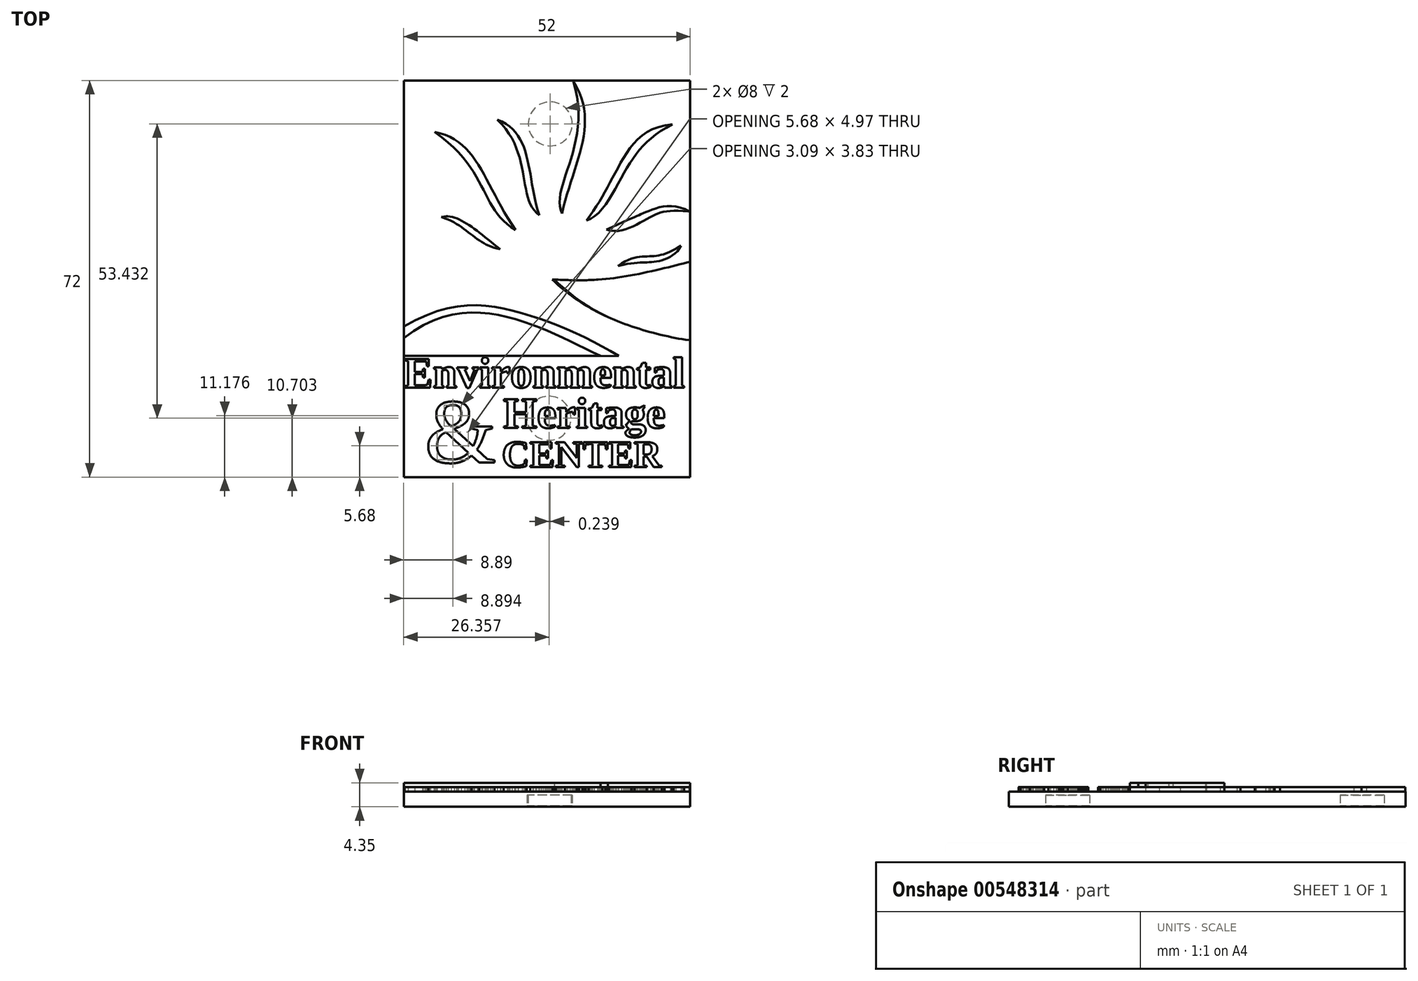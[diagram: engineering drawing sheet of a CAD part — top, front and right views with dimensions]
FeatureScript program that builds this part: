
annotation { "Feature Type Name" : "Feature", "Feature Type Description" : "" }
export const myFeature = defineFeature(function(context is Context, id is Id, definition is map)
    precondition{}
    {
        {
            var Q0;
            Q0=qCreatedBy(makeId("Top.planeOp"),FACE);
            var sketch = newSketch(context, id + "F0", { "sketchPlane" : qUnion([Q0])});
            skFitSpline(sketch, "E0", {"points": [v(4.31, 44.96) * mm, v(2.38, 20.78) * mm], "startDerivative": vector(14.8, -23.62) * mm, "endDerivative": vector(-6, -27.25) * mm});
            skFitSpline(sketch, "E1", {"points": [v(4.31, 45.15) * mm, v(2.38, 20.78) * mm], "startDerivative": vector(10.64, -35.08) * mm, "endDerivative": vector(7.02, -14.4) * mm});
            skFitSpline(sketch, "E2", {"points": [v(-9.33, 37.79) * mm, v(-1.76, 20.42) * mm], "startDerivative": vector(19.64, -7.65) * mm, "endDerivative": vector(7, -21.6) * mm});
            skFitSpline(sketch, "E3", {"points": [v(-9.33, 37.79) * mm, v(-1.76, 20.42) * mm], "startDerivative": vector(19.52, -19.07) * mm, "endDerivative": vector(12.52, -9.58) * mm});
            skFitSpline(sketch, "E4", {"points": [v(-20.73, 35.54) * mm, v(-6.05, 17.77) * mm], "startDerivative": vector(23.87, -4.4) * mm, "endDerivative": vector(17.15, -24.68) * mm});
            skFitSpline(sketch, "E5", {"points": [v(-20.73, 35.54) * mm, v(-6.05, 17.77) * mm], "startDerivative": vector(30.6, -21.67) * mm, "endDerivative": vector(19.93, -11.59) * mm});
            skFitSpline(sketch, "E6", {"points": [v(-19.49, 20.1) * mm, v(-8.88, 14.3) * mm], "startDerivative": vector(8.74, 2.48) * mm, "endDerivative": vector(12.97, -10.2) * mm});
            skFitSpline(sketch, "E7", {"points": [v(-19.49, 20.1) * mm, v(-8.88, 14.3) * mm], "startDerivative": vector(14.35, -4.5) * mm, "endDerivative": vector(12.97, -1.93) * mm});
            skFitSpline(sketch, "E8", {"points": [v(22.42, 36.91) * mm, v(12.63, 29.23) * mm, v(6.82, 19.5) * mm], "startDerivative": vector(-32.02, -1.89) * mm, "endDerivative": vector(-15.34, -19.87) * mm});
            skFitSpline(sketch, "E9", {"points": [v(22.42, 36.91) * mm, v(13.78, 28.37) * mm, v(6.82, 19.5) * mm], "startDerivative": vector(-26.44, -13.49) * mm, "endDerivative": vector(-18.51, -5.76) * mm});
            skFitSpline(sketch, "E10", {"points": [v(10.44, 17.8) * mm, v(17.32, 20.88) * mm, v(25.87, 20.74) * mm], "startDerivative": vector(29.68, 13.68) * mm, "endDerivative": vector(18.14, -14.7) * mm});
            skFitSpline(sketch, "E11", {"points": [v(10.44, 17.8) * mm, v(18.21, 19.99) * mm, v(25.38, 21.1) * mm], "startDerivative": vector(15.53, -5.4) * mm, "endDerivative": vector(24.63, -2.44) * mm});
            skFitSpline(sketch, "E12", {"points": [v(12.53, 11.24) * mm, v(18.58, 12.99) * mm, v(23.97, 14.92) * mm], "startDerivative": vector(15.39, 11.11) * mm, "endDerivative": vector(14.79, 9.41) * mm});
            skFitSpline(sketch, "E13", {"points": [v(12.53, 11.24) * mm, v(18.98, 11.97) * mm, v(23.97, 14.92) * mm], "startDerivative": vector(21.7, 4.9) * mm, "endDerivative": vector(6.08, 13.06) * mm});
            skFitSpline(sketch, "E14", {"points": [v(0.27, 8.75) * mm, v(10.37, 1.93) * mm, v(25.63, -2.36) * mm], "startDerivative": vector(17.78, -17.12) * mm, "endDerivative": vector(27.14, -3.63) * mm});
            skFitSpline(sketch, "E15", {"points": [v(-1.66, 8.98) * mm, v(10.04, 0.8) * mm, v(25.63, -3.6) * mm], "startDerivative": vector(19.98, -21.9) * mm, "endDerivative": vector(27.82, -3.65) * mm});
            skFitSpline(sketch, "E16", {"points": [v(0.27, 8.75) * mm, v(12.27, 9.1) * mm, v(25.68, 12.08) * mm], "startDerivative": vector(25.56, -1.26) * mm, "endDerivative": vector(20.03, 5.21) * mm});
            skFitSpline(sketch, "E17", {"points": [v(-26.4, 0.32) * mm, v(-5.28, 2.75) * mm, v(12.45, -5.04) * mm], "startDerivative": vector(42.56, 27.28) * mm, "endDerivative": vector(34.62, -19.88) * mm});
            skFitSpline(sketch, "E18", {"points": [v(-26.4, -2.02) * mm, v(-5.58, 1.45) * mm, v(9.78, -5.04) * mm], "startDerivative": vector(33.71, 28.86) * mm, "endDerivative": vector(32.46, -15.17) * mm});
            skFitSpline(sketch, "E19", {"points": [v(-26.4, 19.28) * mm, v(-13.06, 11.61) * mm, v(-1.66, 8.98) * mm], "startDerivative": vector(29.42, -19.76) * mm, "endDerivative": vector(24.53, -2.4) * mm});
            skFitSpline(sketch, "E20", {"points": [v(-8, 10.03) * mm, v(0.62, 16.74) * mm, v(8.95, 8.75) * mm], "startDerivative": vector(8.7, 30.35) * mm, "endDerivative": vector(2.28, -31.65) * mm});
            skLineSegment(sketch, "E21", {"start": v(-26.4, 44.96) * mm, "end": v(-26.4, -5.04) * mm});
            skLineSegment(sketch, "E22", {"start": v(-26.4, 44.96) * mm, "end": v(4.33, 44.96) * mm});
            skLineSegment(sketch, "E23", {"start": v(-26.4, -5.04) * mm, "end": v(25.6, -5.04) * mm});
            skLineSegment(sketch, "E24.trimOffspring", {"start": v(4.33, 44.96) * mm, "end": v(25.6, 44.96) * mm});
            skLineSegment(sketch, "E25", {"start": v(25.6, 44.96) * mm, "end": v(25.6, -5.04) * mm});
            skText(sketch, "E26", { "text": "Environmental", "fontName": "Tinos-Regular.ttf"});
            skText(sketch, "E27", { "text": "Heritage", "fontName": "Tinos-Regular.ttf"});
            skText(sketch, "E28", { "text": "C E N T E R", "fontName": "Tinos-Regular.ttf"});
            skText(sketch, "E29", { "text": "&", "fontName": "Tinos-Regular.ttf"});
            skLineSegment(sketch, "E30", {"start": v(-26.4, -5.04) * mm, "end": v(-26.4, -27.04) * mm});
            skLineSegment(sketch, "E31", {"start": v(25.6, -5.04) * mm, "end": v(25.6, -27.04) * mm});
            skLineSegment(sketch, "E32", {"start": v(-26.4, -27.04) * mm, "end": v(25.6, -27.04) * mm});
            const initialGuessF0  = {"E26": [-0.0253, -0.01139, 1, 0, 0.006], "E27": [-0.00842, -0.0183, 1, 0, 0.006], "E28": [-0.0084, -0.0244, 1, 0, 0.004], "E29": [-0.02253, -0.02446, 1, 0, 0.012]};
            skSetInitialGuess(sketch, initialGuessF0);
            skSolve(sketch);
        }
        {
            var Q0;
            Q0=makeQuery(id+"F0.imprint","IMPRINT",FACE,{"disambiguationData":[TD([[makeQuery(id+"F0.imprint","IMPRINT",EDGE,{"derivedFrom":sQuery(id+"F0.wireOp",EDGE,"E26.sketch_text.stroke-270")}),1.0]])]});
            var Q1;
            Q1=makeQuery(id+"F0.imprint","IMPRINT",FACE,{"disambiguationData":[TD([[makeQuery(id+"F0.imprint","IMPRINT",EDGE,{"derivedFrom":sQuery(id+"F0.wireOp",EDGE,"E10")}),-1.0]])]});
            var Q2;
            Q2=makeQuery(id+"F0.imprint","IMPRINT",FACE,{"disambiguationData":[TD([[makeQuery(id+"F0.imprint","IMPRINT",EDGE,{"derivedFrom":sQuery(id+"F0.wireOp",EDGE,"E26.sketch_text.stroke-205")}),-1.0]])]});
            var Q3;
            Q3=makeQuery(id+"F0.imprint","IMPRINT",FACE,{"disambiguationData":[TD([[makeQuery(id+"F0.imprint","IMPRINT",EDGE,{"derivedFrom":sQuery(id+"F0.wireOp",EDGE,"E26.sketch_text.stroke-200")}),1.0]])]});
            var Q4;
            Q4=makeQuery(id+"F0.imprint","IMPRINT",FACE,{"disambiguationData":[TD([[makeQuery(id+"F0.imprint","IMPRINT",EDGE,{"derivedFrom":sQuery(id+"F0.wireOp",EDGE,"E26.sketch_text.stroke-51")}),-1.0]])]});
            var Q5;
            {var subQ1=sQuery(id+"F0.wireOp",EDGE,"E15");Q5=makeQuery(id+"F0.imprint","IMPRINT",FACE,{"disambiguationData":[TD([[makeQuery(id+"F0.imprint","IMPRINT",EDGE,{"derivedFrom":subQ1}),-1.0]])]});}
            var Q6;
            Q6=makeQuery(id+"F0.imprint","IMPRINT",FACE,{"disambiguationData":[TD([[makeQuery(id+"F0.imprint","IMPRINT",EDGE,{"derivedFrom":sQuery(id+"F0.wireOp",EDGE,"E27.sketch_text.stroke-161")}),1.0]])]});
            var Q7;
            Q7=makeQuery(id+"F0.imprint","IMPRINT",FACE,{"disambiguationData":[TD([[makeQuery(id+"F0.imprint","IMPRINT",EDGE,{"derivedFrom":sQuery(id+"F0.wireOp",EDGE,"E26.sketch_text.stroke-103")}),-1.0]])]});
            var Q8;
            {var subQ0=sQuery(id+"F0.wireOp",EDGE,"E1");var subQ1=sQuery(id+"F0.wireOp",EDGE,"E0");var subQ2=makeQuery(id+"F0.imprint","INTERSECT",VERTEX,{"disambiguationData":[OD(0.0)],"derivedFrom":[subQ1,subQ0]});Q8=makeQuery(id+"F0.imprint","IMPRINT",FACE,{"disambiguationData":[TD([[makeQuery(id+"F0.imprint","IMPRINT",EDGE,{"disambiguationData":[TD([[subQ2,1.0]])],"derivedFrom":subQ1}),-1.0]])]});}
            var Q9;
            Q9=makeQuery(id+"F0.imprint","IMPRINT",FACE,{"disambiguationData":[TD([[makeQuery(id+"F0.imprint","IMPRINT",EDGE,{"derivedFrom":sQuery(id+"F0.wireOp",EDGE,"E4")}),-1.0]])]});
            var Q10;
            Q10=makeQuery(id+"F0.imprint","IMPRINT",FACE,{"disambiguationData":[TD([[makeQuery(id+"F0.imprint","IMPRINT",EDGE,{"derivedFrom":sQuery(id+"F0.wireOp",EDGE,"E2")}),-1.0]])]});
            var Q11;
            {var subQ4=sQuery(id+"F0.wireOp",EDGE,"E14");Q11=makeQuery(id+"F0.imprint","IMPRINT",FACE,{"disambiguationData":[TD([[makeQuery(id+"F0.imprint","IMPRINT",EDGE,{"derivedFrom":subQ4}),-1.0]])]});}
            var Q12;
            Q12=makeQuery(id+"F0.imprint","IMPRINT",FACE,{"disambiguationData":[TD([[makeQuery(id+"F0.imprint","IMPRINT",EDGE,{"derivedFrom":sQuery(id+"F0.wireOp",EDGE,"E26.sketch_text.stroke-26")}),-1.0]])]});
            var Q13;
            Q13=makeQuery(id+"F0.imprint","IMPRINT",FACE,{"disambiguationData":[TD([[makeQuery(id+"F0.imprint","IMPRINT",EDGE,{"derivedFrom":sQuery(id+"F0.wireOp",EDGE,"E29.sketch_text.stroke-0")}),-1.0]])]});
            var Q14;
            Q14=makeQuery(id+"F0.imprint","IMPRINT",FACE,{"disambiguationData":[TD([[makeQuery(id+"F0.imprint","IMPRINT",EDGE,{"derivedFrom":sQuery(id+"F0.wireOp",EDGE,"E12")}),-1.0]])]});
            var Q15;
            Q15=makeQuery(id+"F0.imprint","IMPRINT",FACE,{"disambiguationData":[TD([[makeQuery(id+"F0.imprint","IMPRINT",EDGE,{"derivedFrom":sQuery(id+"F0.wireOp",EDGE,"E29.sketch_text.stroke-34")}),1.0]])]});
            var Q16;
            Q16=makeQuery(id+"F0.imprint","IMPRINT",FACE,{"disambiguationData":[TD([[makeQuery(id+"F0.imprint","IMPRINT",EDGE,{"derivedFrom":sQuery(id+"F0.wireOp",EDGE,"E26.sketch_text.stroke-110")}),1.0]])]});
            var Q17;
            {var subQ0=sQuery(id+"F0.wireOp",EDGE,"E14");Q17=makeQuery(id+"F0.imprint","IMPRINT",FACE,{"disambiguationData":[TD([[makeQuery(id+"F0.imprint","IMPRINT",EDGE,{"derivedFrom":subQ0}),1.0]])]});}
            var Q18;
            {var subQ0=sQuery(id+"F0.wireOp",EDGE,"E18");Q18=makeQuery(id+"F0.imprint","IMPRINT",FACE,{"disambiguationData":[TD([[makeQuery(id+"F0.imprint","IMPRINT",EDGE,{"derivedFrom":subQ0}),-1.0]])]});}
            var Q19;
            Q19=makeQuery(id+"F0.imprint","IMPRINT",FACE,{"disambiguationData":[TD([[makeQuery(id+"F0.imprint","IMPRINT",EDGE,{"derivedFrom":sQuery(id+"F0.wireOp",EDGE,"E27.sketch_text.stroke-170")}),1.0]])]});
            var Q20;
            Q20=makeQuery(id+"F0.imprint","IMPRINT",FACE,{"disambiguationData":[TD([[makeQuery(id+"F0.imprint","IMPRINT",EDGE,{"derivedFrom":sQuery(id+"F0.wireOp",EDGE,"E28.sketch_text.stroke-131")}),1.0]])]});
            var Q21;
            Q21=makeQuery(id+"F0.imprint","IMPRINT",FACE,{"disambiguationData":[TD([[makeQuery(id+"F0.imprint","IMPRINT",EDGE,{"derivedFrom":sQuery(id+"F0.wireOp",EDGE,"E6")}),-1.0]])]});
            var Q22;
            Q22=makeQuery(id+"F0.imprint","IMPRINT",FACE,{"disambiguationData":[TD([[makeQuery(id+"F0.imprint","IMPRINT",EDGE,{"derivedFrom":sQuery(id+"F0.wireOp",EDGE,"E29.sketch_text.stroke-28")}),1.0]])]});
            var Q23;
            Q23=makeQuery(id+"F0.imprint","IMPRINT",FACE,{"disambiguationData":[TD([[makeQuery(id+"F0.imprint","IMPRINT",EDGE,{"derivedFrom":sQuery(id+"F0.wireOp",EDGE,"E26.sketch_text.stroke-0")}),1.0]])]});
            var Q24;
            Q24=makeQuery(id+"F0.imprint","IMPRINT",FACE,{"disambiguationData":[TD([[makeQuery(id+"F0.imprint","IMPRINT",EDGE,{"derivedFrom":sQuery(id+"F0.wireOp",EDGE,"E27.sketch_text.stroke-126")}),1.0]])]});
            var Q25;
            Q25=makeQuery(id+"F0.imprint","IMPRINT",FACE,{"disambiguationData":[TD([[makeQuery(id+"F0.imprint","IMPRINT",EDGE,{"derivedFrom":sQuery(id+"F0.wireOp",EDGE,"E2")}),1.0]])]});
            var Q26;
            Q26=makeQuery(id+"F0.imprint","IMPRINT",FACE,{"disambiguationData":[TD([[makeQuery(id+"F0.imprint","IMPRINT",EDGE,{"derivedFrom":sQuery(id+"F0.wireOp",EDGE,"E27.sketch_text.stroke-44")}),1.0]])]});
            var Q27;
            Q27=makeQuery(id+"F0.imprint","IMPRINT",FACE,{"disambiguationData":[TD([[makeQuery(id+"F0.imprint","IMPRINT",EDGE,{"derivedFrom":sQuery(id+"F0.wireOp",EDGE,"E8")}),1.0]])]});
            var Q28;
            Q28=makeQuery(id+"F0.imprint","IMPRINT",FACE,{"disambiguationData":[TD([[makeQuery(id+"F0.imprint","IMPRINT",EDGE,{"derivedFrom":sQuery(id+"F0.wireOp",EDGE,"E27.sketch_text.stroke-194")}),1.0]])]});
            var Q29;
            {var subQ0=sQuery(id+"F0.wireOp",EDGE,"E17");Q29=makeQuery(id+"F0.imprint","IMPRINT",FACE,{"disambiguationData":[TD([[makeQuery(id+"F0.imprint","IMPRINT",EDGE,{"derivedFrom":subQ0}),-1.0]])]});}
            var Q30;
            Q30=makeQuery(id+"F0.imprint","IMPRINT",FACE,{"disambiguationData":[TD([[makeQuery(id+"F0.imprint","IMPRINT",EDGE,{"derivedFrom":sQuery(id+"F0.wireOp",EDGE,"E26.sketch_text.stroke-277")}),-1.0]])]});
            var Q31;
            Q31=makeQuery(id+"F0.imprint","IMPRINT",FACE,{"disambiguationData":[TD([[makeQuery(id+"F0.imprint","IMPRINT",EDGE,{"derivedFrom":sQuery(id+"F0.wireOp",EDGE,"E27.sketch_text.stroke-0")}),-1.0]])]});
            var Q32;
            Q32=makeQuery(id+"F0.imprint","IMPRINT",FACE,{"disambiguationData":[TD([[makeQuery(id+"F0.imprint","IMPRINT",EDGE,{"derivedFrom":sQuery(id+"F0.wireOp",EDGE,"E28.sketch_text.stroke-20")}),-1.0]])]});
            var Q33;
            Q33=makeQuery(id+"F0.imprint","IMPRINT",FACE,{"disambiguationData":[TD([[makeQuery(id+"F0.imprint","IMPRINT",EDGE,{"derivedFrom":sQuery(id+"F0.wireOp",EDGE,"E26.sketch_text.stroke-249")}),-1.0]])]});
            var Q34;
            Q34=makeQuery(id+"F0.imprint","IMPRINT",FACE,{"disambiguationData":[TD([[makeQuery(id+"F0.imprint","IMPRINT",EDGE,{"derivedFrom":sQuery(id+"F0.wireOp",EDGE,"E26.sketch_text.stroke-0")}),-1.0]])]});
            var Q35;
            Q35=makeQuery(id+"F0.imprint","IMPRINT",FACE,{"disambiguationData":[TD([[makeQuery(id+"F0.imprint","IMPRINT",EDGE,{"derivedFrom":sQuery(id+"F0.wireOp",EDGE,"E26.sketch_text.stroke-74")}),-1.0]])]});
            var Q36;
            Q36=makeQuery(id+"F0.imprint","IMPRINT",FACE,{"disambiguationData":[TD([[makeQuery(id+"F0.imprint","IMPRINT",EDGE,{"derivedFrom":sQuery(id+"F0.wireOp",EDGE,"E26.sketch_text.stroke-184")}),-1.0]])]});
            var Q37;
            Q37=makeQuery(id+"F0.imprint","IMPRINT",FACE,{"disambiguationData":[TD([[makeQuery(id+"F0.imprint","IMPRINT",EDGE,{"derivedFrom":sQuery(id+"F0.wireOp",EDGE,"E27.sketch_text.stroke-28")}),-1.0]])]});
            var Q38;
            Q38=makeQuery(id+"F0.imprint","IMPRINT",FACE,{"disambiguationData":[TD([[makeQuery(id+"F0.imprint","IMPRINT",EDGE,{"derivedFrom":sQuery(id+"F0.wireOp",EDGE,"E26.sketch_text.stroke-66")}),-1.0]])]});
            var Q39;
            Q39=makeQuery(id+"F0.imprint","IMPRINT",FACE,{"disambiguationData":[TD([[makeQuery(id+"F0.imprint","IMPRINT",EDGE,{"derivedFrom":sQuery(id+"F0.wireOp",EDGE,"E27.sketch_text.stroke-76")}),-1.0]])]});
            var Q40;
            Q40=makeQuery(id+"F0.imprint","IMPRINT",FACE,{"disambiguationData":[TD([[makeQuery(id+"F0.imprint","IMPRINT",EDGE,{"derivedFrom":sQuery(id+"F0.wireOp",EDGE,"E26.sketch_text.stroke-84")}),-1.0]])]});
            var Q41;
            Q41=makeQuery(id+"F0.imprint","IMPRINT",FACE,{"disambiguationData":[TD([[makeQuery(id+"F0.imprint","IMPRINT",EDGE,{"derivedFrom":sQuery(id+"F0.wireOp",EDGE,"E26.sketch_text.stroke-143")}),-1.0]])]});
            var Q42;
            Q42=makeQuery(id+"F0.imprint","IMPRINT",FACE,{"disambiguationData":[TD([[makeQuery(id+"F0.imprint","IMPRINT",EDGE,{"derivedFrom":sQuery(id+"F0.wireOp",EDGE,"E27.sketch_text.stroke-105")}),-1.0]])]});
            var Q43;
            Q43=makeQuery(id+"F0.imprint","IMPRINT",FACE,{"disambiguationData":[TD([[makeQuery(id+"F0.imprint","IMPRINT",EDGE,{"derivedFrom":sQuery(id+"F0.wireOp",EDGE,"E27.sketch_text.stroke-178")}),-1.0]])]});
            var Q44;
            Q44=makeQuery(id+"F0.imprint","IMPRINT",FACE,{"disambiguationData":[TD([[makeQuery(id+"F0.imprint","IMPRINT",EDGE,{"derivedFrom":sQuery(id+"F0.wireOp",EDGE,"E27.sketch_text.stroke-68")}),-1.0]])]});
            var Q45;
            Q45=makeQuery(id+"F0.imprint","IMPRINT",FACE,{"disambiguationData":[TD([[makeQuery(id+"F0.imprint","IMPRINT",EDGE,{"derivedFrom":sQuery(id+"F0.wireOp",EDGE,"E27.sketch_text.stroke-86")}),-1.0]])]});
            var Q46;
            Q46=makeQuery(id+"F0.imprint","IMPRINT",FACE,{"disambiguationData":[TD([[makeQuery(id+"F0.imprint","IMPRINT",EDGE,{"derivedFrom":sQuery(id+"F0.wireOp",EDGE,"E27.sketch_text.stroke-49")}),-1.0]])]});
            var Q47;
            Q47=makeQuery(id+"F0.imprint","IMPRINT",FACE,{"disambiguationData":[TD([[makeQuery(id+"F0.imprint","IMPRINT",EDGE,{"derivedFrom":sQuery(id+"F0.wireOp",EDGE,"E28.sketch_text.stroke-85")}),-1.0]])]});
            var Q48;
            Q48=makeQuery(id+"F0.imprint","IMPRINT",FACE,{"disambiguationData":[TD([[makeQuery(id+"F0.imprint","IMPRINT",EDGE,{"derivedFrom":sQuery(id+"F0.wireOp",EDGE,"E28.sketch_text.stroke-46")}),-1.0]])]});
            var Q49;
            Q49=makeQuery(id+"F0.imprint","IMPRINT",FACE,{"disambiguationData":[TD([[makeQuery(id+"F0.imprint","IMPRINT",EDGE,{"derivedFrom":sQuery(id+"F0.wireOp",EDGE,"E26.sketch_text.stroke-230")}),-1.0]])]});
            var Q50;
            Q50=makeQuery(id+"F0.imprint","IMPRINT",FACE,{"disambiguationData":[TD([[makeQuery(id+"F0.imprint","IMPRINT",EDGE,{"derivedFrom":sQuery(id+"F0.wireOp",EDGE,"E27.sketch_text.stroke-133")}),-1.0]])]});
            var Q51;
            Q51=makeQuery(id+"F0.imprint","IMPRINT",FACE,{"disambiguationData":[TD([[makeQuery(id+"F0.imprint","IMPRINT",EDGE,{"derivedFrom":sQuery(id+"F0.wireOp",EDGE,"E28.sketch_text.stroke-0")}),-1.0]])]});
            var Q52;
            Q52=makeQuery(id+"F0.imprint","IMPRINT",FACE,{"disambiguationData":[TD([[makeQuery(id+"F0.imprint","IMPRINT",EDGE,{"derivedFrom":sQuery(id+"F0.wireOp",EDGE,"E26.sketch_text.stroke-118")}),-1.0]])]});
            var Q53;
            Q53=makeQuery(id+"F0.imprint","IMPRINT",FACE,{"disambiguationData":[TD([[makeQuery(id+"F0.imprint","IMPRINT",EDGE,{"derivedFrom":sQuery(id+"F0.wireOp",EDGE,"E28.sketch_text.stroke-111")}),-1.0]])]});
            var Q54;
            Q54=makeQuery(id+"F0.imprint","IMPRINT",FACE,{"disambiguationData":[TD([[makeQuery(id+"F0.imprint","IMPRINT",EDGE,{"derivedFrom":sQuery(id+"F0.wireOp",EDGE,"E28.sketch_text.stroke-66")}),-1.0]])]});
            var Q55;
            {var subQ0=sQuery(id+"F0.wireOp",EDGE,"E22");var subQ1=sQuery(id+"F0.wireOp",EDGE,"E0");var subQ2=makeQuery(id+"F0.imprint","INTERSECT",VERTEX,{"derivedFrom":[subQ1,subQ0]});Q55=makeQuery(id+"F0.imprint","IMPRINT",FACE,{"disambiguationData":[TD([[makeQuery(id+"F0.imprint","IMPRINT",EDGE,{"disambiguationData":[TD([[subQ2,-1.0]])],"derivedFrom":subQ1}),1.0]])]});}
            extrude(context, id + "F1", {"entities" : qUnion([Q0, Q1, Q2, Q3, Q4, Q5, Q6, Q7, Q8, Q9, Q10, Q11, Q12, Q13, Q14, Q15, Q16, Q17, Q18, Q19, Q20, Q21, Q22, Q23, Q24, Q25, Q26, Q27, Q28, Q29, Q30, Q31, Q32, Q33, Q34, Q35, Q36, Q37, Q38, Q39, Q40, Q41, Q42, Q43, Q44, Q45, Q46, Q47, Q48, Q49, Q50, Q51, Q52, Q53, Q54, Q55]), "depth" : 2.75 * mm, "offsetDistance" : 25 * mm});
        }
        {
            var Q0;
            Q0=makeQuery(id+"F1.opExtrude","CAP_FACE",FACE,{"disambiguationData":[OSD([sQuery(id+"F0.wireOp",EDGE,"E21"),sQuery(id+"F0.wireOp",EDGE,"E22"),sQuery(id+"F0.wireOp",EDGE,"E24.trimOffspring"),sQuery(id+"F0.wireOp",EDGE,"E25"),sQuery(id+"F0.wireOp",EDGE,"E30"),sQuery(id+"F0.wireOp",EDGE,"E31"),sQuery(id+"F0.wireOp",EDGE,"E32")])],"isStart":false});
            var sketch = newSketch(context, id + "F2", { "sketchPlane" : qUnion([Q0])});
            skFitSpline(sketch, "E33", {"points": [v(4.38, 44.9) * mm, v(2.33, 20.86) * mm], "startDerivative": vector(14.8, -23.62) * mm, "endDerivative": vector(-6, -27.25) * mm});
            skFitSpline(sketch, "E34", {"points": [v(4.38, 44.9) * mm, v(2.33, 20.86) * mm], "startDerivative": vector(10.64, -35.08) * mm, "endDerivative": vector(7.02, -14.4) * mm});
            skFitSpline(sketch, "E35", {"points": [v(-9.38, 37.87) * mm, v(-1.81, 20.5) * mm], "startDerivative": vector(19.64, -7.65) * mm, "endDerivative": vector(7, -21.6) * mm});
            skFitSpline(sketch, "E36", {"points": [v(-9.38, 37.87) * mm, v(-1.81, 20.5) * mm], "startDerivative": vector(19.52, -19.07) * mm, "endDerivative": vector(12.52, -9.58) * mm});
            skFitSpline(sketch, "E37", {"points": [v(-20.78, 35.62) * mm, v(-6.1, 17.85) * mm], "startDerivative": vector(23.87, -4.4) * mm, "endDerivative": vector(17.15, -24.68) * mm});
            skFitSpline(sketch, "E38", {"points": [v(-20.78, 35.62) * mm, v(-6.1, 17.85) * mm], "startDerivative": vector(30.6, -21.67) * mm, "endDerivative": vector(19.93, -11.59) * mm});
            skFitSpline(sketch, "E39", {"points": [v(-19.54, 20.17) * mm, v(-8.93, 14.38) * mm], "startDerivative": vector(8.74, 2.48) * mm, "endDerivative": vector(12.97, -10.2) * mm});
            skFitSpline(sketch, "E40", {"points": [v(-19.54, 20.17) * mm, v(-8.93, 14.38) * mm], "startDerivative": vector(14.35, -4.5) * mm, "endDerivative": vector(12.97, -1.93) * mm});
            skFitSpline(sketch, "E41", {"points": [v(22.36, 37) * mm, v(12.58, 29.31) * mm, v(6.77, 19.58) * mm], "startDerivative": vector(-32.02, -1.89) * mm, "endDerivative": vector(-15.34, -19.87) * mm});
            skFitSpline(sketch, "E42", {"points": [v(22.36, 37) * mm, v(13.73, 28.45) * mm, v(6.77, 19.58) * mm], "startDerivative": vector(-26.44, -13.49) * mm, "endDerivative": vector(-18.51, -5.76) * mm});
            skFitSpline(sketch, "E43", {"points": [v(10.4, 17.89) * mm, v(17.26, 20.96) * mm, v(25.82, 20.82) * mm], "startDerivative": vector(29.68, 13.68) * mm, "endDerivative": vector(18.14, -14.7) * mm});
            skFitSpline(sketch, "E44", {"points": [v(10.4, 17.89) * mm, v(18.16, 20.07) * mm, v(25.33, 21.18) * mm], "startDerivative": vector(15.53, -5.4) * mm, "endDerivative": vector(24.63, -2.44) * mm});
            skFitSpline(sketch, "E45", {"points": [v(12.47, 11.32) * mm, v(18.53, 13.07) * mm, v(23.92, 15) * mm], "startDerivative": vector(15.39, 11.11) * mm, "endDerivative": vector(14.79, 9.41) * mm});
            skFitSpline(sketch, "E46", {"points": [v(12.47, 11.32) * mm, v(18.93, 12.05) * mm, v(23.92, 15) * mm], "startDerivative": vector(21.7, 4.9) * mm, "endDerivative": vector(6.08, 13.06) * mm});
            skFitSpline(sketch, "E47", {"points": [v(0.55, 8.85) * mm, v(10.65, 2.03) * mm, v(25.9, -2.26) * mm], "startDerivative": vector(17.78, -17.12) * mm, "endDerivative": vector(27.14, -3.63) * mm});
            skFitSpline(sketch, "E48", {"points": [v(-1.57, 9.02) * mm, v(10.13, 0.84) * mm, v(25.71, -3.56) * mm], "startDerivative": vector(19.98, -21.9) * mm, "endDerivative": vector(27.82, -3.65) * mm});
            skFitSpline(sketch, "E49", {"points": [v(0.55, 8.85) * mm, v(12.55, 9.21) * mm, v(25.96, 12.19) * mm], "startDerivative": vector(25.56, -1.26) * mm, "endDerivative": vector(20.03, 5.21) * mm});
            skFitSpline(sketch, "E50", {"points": [v(-26.4, 0.3) * mm, v(-5.5, 2.89) * mm, v(12.62, -5.04) * mm], "startDerivative": vector(49.7, 29.2) * mm, "endDerivative": vector(34.07, -20.85) * mm});
            skFitSpline(sketch, "E51", {"points": [v(-26.4, -1.8) * mm, v(-5.5, 1.57) * mm, v(9.7, -5.05) * mm], "startDerivative": vector(41.22, 32.93) * mm, "endDerivative": vector(32.46, -15.17) * mm});
            skFitSpline(sketch, "E52", {"points": [v(-26.4, 19.3) * mm, v(-12.97, 11.65) * mm, v(-1.57, 9.02) * mm], "startDerivative": vector(29.42, -19.76) * mm, "endDerivative": vector(24.53, -2.4) * mm});
            skFitSpline(sketch, "E53", {"points": [v(-8.06, 10.11) * mm, v(0.57, 16.82) * mm, v(8.9, 8.83) * mm], "startDerivative": vector(8.7, 30.35) * mm, "endDerivative": vector(2.28, -31.65) * mm});
            skLineSegment(sketch, "E54", {"start": v(-26.4, 44.96) * mm, "end": v(-26.4, -5.07) * mm});
            skLineSegment(sketch, "E55", {"start": v(-26.4, 44.96) * mm, "end": v(25.57, 44.96) * mm});
            skLineSegment(sketch, "E56", {"start": v(-26.4, -5.07) * mm, "end": v(25.6, -5.04) * mm});
            skLineSegment(sketch, "E57", {"start": v(25.57, 44.96) * mm, "end": v(25.6, -5.04) * mm});
            skText(sketch, "E58", { "text": "Environmental", "fontName": "Tinos-Bold.ttf"});
            skText(sketch, "E59", { "text": "Heritage", "fontName": "Tinos-Bold.ttf"});
            skText(sketch, "E60", { "text": "CENTER", "fontName": "Tinos-Bold.ttf"});
            skText(sketch, "E61", { "text": "&", "fontName": "Tinos-Regular.ttf"});
            skLineSegment(sketch, "E62", {"start": v(-26.4, -5.07) * mm, "end": v(-26.4, -27.07) * mm});
            skLineSegment(sketch, "E63", {"start": v(25.6, -5.04) * mm, "end": v(25.6, -27.07) * mm});
            skLineSegment(sketch, "E64", {"start": v(-26.4, -27.07) * mm, "end": v(25.6, -27.07) * mm});
            const initialGuessF2  = {"E58": [-0.0264, -0.01077, 1, 0, 0.0057], "E59": [-0.00835, -0.0181, 1, 0, 0.0057], "E60": [-0.00858, -0.02523, 1, 0, 0.005], "E61": [-0.02258, -0.02438, 1, 0, 0.012]};
            skSetInitialGuess(sketch, initialGuessF2);
            skSolve(sketch);
        }
        {
            var Q0;
            Q0=makeQuery(id+"F2.imprint","IMPRINT",FACE,{"disambiguationData":[TD([[makeQuery(id+"F2.imprint","IMPRINT",EDGE,{"derivedFrom":sQuery(id+"F2.wireOp",EDGE,"E61.sketch_text.stroke-0")}),-1.0]])]});
            var Q1;
            Q1=makeQuery(id+"F2.imprint","IMPRINT",FACE,{"disambiguationData":[TD([[makeQuery(id+"F2.imprint","IMPRINT",EDGE,{"derivedFrom":sQuery(id+"F2.wireOp",EDGE,"E59.sketch_text.stroke-0")}),-1.0]])]});
            var Q2;
            Q2=makeQuery(id+"F2.imprint","IMPRINT",FACE,{"disambiguationData":[TD([[makeQuery(id+"F2.imprint","IMPRINT",EDGE,{"derivedFrom":sQuery(id+"F2.wireOp",EDGE,"E59.sketch_text.stroke-28")}),-1.0]])]});
            var Q3;
            Q3=makeQuery(id+"F2.imprint","IMPRINT",FACE,{"disambiguationData":[TD([[makeQuery(id+"F2.imprint","IMPRINT",EDGE,{"derivedFrom":sQuery(id+"F2.wireOp",EDGE,"E59.sketch_text.stroke-49")}),-1.0]])]});
            var Q4;
            Q4=makeQuery(id+"F2.imprint","IMPRINT",FACE,{"disambiguationData":[TD([[makeQuery(id+"F2.imprint","IMPRINT",EDGE,{"derivedFrom":sQuery(id+"F2.wireOp",EDGE,"E58.sketch_text.stroke-118")}),-1.0]])]});
            var Q5;
            Q5=makeQuery(id+"F2.imprint","IMPRINT",FACE,{"disambiguationData":[TD([[makeQuery(id+"F2.imprint","IMPRINT",EDGE,{"derivedFrom":sQuery(id+"F2.wireOp",EDGE,"E58.sketch_text.stroke-103")}),-1.0]])]});
            var Q6;
            Q6=makeQuery(id+"F2.imprint","IMPRINT",FACE,{"disambiguationData":[TD([[makeQuery(id+"F2.imprint","IMPRINT",EDGE,{"derivedFrom":sQuery(id+"F2.wireOp",EDGE,"E58.sketch_text.stroke-84")}),-1.0]])]});
            var Q7;
            Q7=makeQuery(id+"F2.imprint","IMPRINT",FACE,{"disambiguationData":[TD([[makeQuery(id+"F2.imprint","IMPRINT",EDGE,{"derivedFrom":sQuery(id+"F2.wireOp",EDGE,"E58.sketch_text.stroke-74")}),-1.0]])]});
            var Q8;
            Q8=makeQuery(id+"F2.imprint","IMPRINT",FACE,{"disambiguationData":[TD([[makeQuery(id+"F2.imprint","IMPRINT",EDGE,{"derivedFrom":sQuery(id+"F2.wireOp",EDGE,"E58.sketch_text.stroke-66")}),-1.0]])]});
            var Q9;
            Q9=makeQuery(id+"F2.imprint","IMPRINT",FACE,{"disambiguationData":[TD([[makeQuery(id+"F2.imprint","IMPRINT",EDGE,{"derivedFrom":sQuery(id+"F2.wireOp",EDGE,"E58.sketch_text.stroke-51")}),-1.0]])]});
            var Q10;
            Q10=makeQuery(id+"F2.imprint","IMPRINT",FACE,{"disambiguationData":[TD([[makeQuery(id+"F2.imprint","IMPRINT",EDGE,{"derivedFrom":sQuery(id+"F2.wireOp",EDGE,"E58.sketch_text.stroke-143")}),-1.0]])]});
            var Q11;
            Q11=makeQuery(id+"F2.imprint","IMPRINT",FACE,{"disambiguationData":[TD([[makeQuery(id+"F2.imprint","IMPRINT",EDGE,{"derivedFrom":sQuery(id+"F2.wireOp",EDGE,"E58.sketch_text.stroke-184")}),-1.0]])]});
            var Q12;
            Q12=makeQuery(id+"F2.imprint","IMPRINT",FACE,{"disambiguationData":[TD([[makeQuery(id+"F2.imprint","IMPRINT",EDGE,{"derivedFrom":sQuery(id+"F2.wireOp",EDGE,"E59.sketch_text.stroke-86")}),-1.0]])]});
            var Q13;
            Q13=makeQuery(id+"F2.imprint","IMPRINT",FACE,{"disambiguationData":[TD([[makeQuery(id+"F2.imprint","IMPRINT",EDGE,{"derivedFrom":sQuery(id+"F2.wireOp",EDGE,"E59.sketch_text.stroke-76")}),-1.0]])]});
            var Q14;
            Q14=makeQuery(id+"F2.imprint","IMPRINT",FACE,{"disambiguationData":[TD([[makeQuery(id+"F2.imprint","IMPRINT",EDGE,{"derivedFrom":sQuery(id+"F2.wireOp",EDGE,"E59.sketch_text.stroke-68")}),-1.0]])]});
            var Q15;
            Q15=makeQuery(id+"F2.imprint","IMPRINT",FACE,{"disambiguationData":[TD([[makeQuery(id+"F2.imprint","IMPRINT",EDGE,{"derivedFrom":sQuery(id+"F2.wireOp",EDGE,"E59.sketch_text.stroke-105")}),-1.0]])]});
            var Q16;
            Q16=makeQuery(id+"F2.imprint","IMPRINT",FACE,{"disambiguationData":[TD([[makeQuery(id+"F2.imprint","IMPRINT",EDGE,{"derivedFrom":sQuery(id+"F2.wireOp",EDGE,"E58.sketch_text.stroke-26")}),-1.0]])]});
            var Q17;
            Q17=makeQuery(id+"F2.imprint","IMPRINT",FACE,{"disambiguationData":[TD([[makeQuery(id+"F2.imprint","IMPRINT",EDGE,{"derivedFrom":sQuery(id+"F2.wireOp",EDGE,"E58.sketch_text.stroke-205")}),-1.0]])]});
            var Q18;
            Q18=makeQuery(id+"F2.imprint","IMPRINT",FACE,{"disambiguationData":[TD([[makeQuery(id+"F2.imprint","IMPRINT",EDGE,{"derivedFrom":sQuery(id+"F2.wireOp",EDGE,"E58.sketch_text.stroke-230")}),-1.0]])]});
            var Q19;
            Q19=makeQuery(id+"F2.imprint","IMPRINT",FACE,{"disambiguationData":[TD([[makeQuery(id+"F2.imprint","IMPRINT",EDGE,{"derivedFrom":sQuery(id+"F2.wireOp",EDGE,"E58.sketch_text.stroke-249")}),-1.0]])]});
            var Q20;
            Q20=makeQuery(id+"F2.imprint","IMPRINT",FACE,{"disambiguationData":[TD([[makeQuery(id+"F2.imprint","IMPRINT",EDGE,{"derivedFrom":sQuery(id+"F2.wireOp",EDGE,"E58.sketch_text.stroke-277")}),-1.0]])]});
            var Q21;
            Q21=makeQuery(id+"F2.imprint","IMPRINT",FACE,{"disambiguationData":[TD([[makeQuery(id+"F2.imprint","IMPRINT",EDGE,{"derivedFrom":sQuery(id+"F2.wireOp",EDGE,"E59.sketch_text.stroke-133")}),-1.0]])]});
            var Q22;
            Q22=makeQuery(id+"F2.imprint","IMPRINT",FACE,{"disambiguationData":[TD([[makeQuery(id+"F2.imprint","IMPRINT",EDGE,{"derivedFrom":sQuery(id+"F2.wireOp",EDGE,"E59.sketch_text.stroke-178")}),-1.0]])]});
            var Q23;
            Q23=makeQuery(id+"F2.imprint","IMPRINT",FACE,{"disambiguationData":[TD([[makeQuery(id+"F2.imprint","IMPRINT",EDGE,{"derivedFrom":sQuery(id+"F2.wireOp",EDGE,"E60.sketch_text.stroke-111")}),-1.0]])]});
            var Q24;
            Q24=makeQuery(id+"F2.imprint","IMPRINT",FACE,{"disambiguationData":[TD([[makeQuery(id+"F2.imprint","IMPRINT",EDGE,{"derivedFrom":sQuery(id+"F2.wireOp",EDGE,"E60.sketch_text.stroke-85")}),-1.0]])]});
            var Q25;
            Q25=makeQuery(id+"F2.imprint","IMPRINT",FACE,{"disambiguationData":[TD([[makeQuery(id+"F2.imprint","IMPRINT",EDGE,{"derivedFrom":sQuery(id+"F2.wireOp",EDGE,"E60.sketch_text.stroke-66")}),-1.0]])]});
            var Q26;
            Q26=makeQuery(id+"F2.imprint","IMPRINT",FACE,{"disambiguationData":[TD([[makeQuery(id+"F2.imprint","IMPRINT",EDGE,{"derivedFrom":sQuery(id+"F2.wireOp",EDGE,"E60.sketch_text.stroke-46")}),-1.0]])]});
            var Q27;
            Q27=makeQuery(id+"F2.imprint","IMPRINT",FACE,{"disambiguationData":[TD([[makeQuery(id+"F2.imprint","IMPRINT",EDGE,{"derivedFrom":sQuery(id+"F2.wireOp",EDGE,"E60.sketch_text.stroke-20")}),-1.0]])]});
            var Q28;
            Q28=makeQuery(id+"F2.imprint","IMPRINT",FACE,{"disambiguationData":[TD([[makeQuery(id+"F2.imprint","IMPRINT",EDGE,{"derivedFrom":sQuery(id+"F2.wireOp",EDGE,"E60.sketch_text.stroke-0")}),-1.0]])]});
            var Q29;
            Q29=makeQuery(id+"F2.imprint","IMPRINT",FACE,{"disambiguationData":[TD([[makeQuery(id+"F2.imprint","IMPRINT",EDGE,{"derivedFrom":sQuery(id+"F2.wireOp",EDGE,"E58.sketch_text.stroke-0")}),-1.0]])]});
            var Q30;
            {var subQ0=sQuery(id+"F2.wireOp",EDGE,"E51");Q30=makeQuery(id+"F2.imprint","IMPRINT",FACE,{"disambiguationData":[TD([[makeQuery(id+"F2.imprint","IMPRINT",EDGE,{"derivedFrom":subQ0}),-1.0]])]});}
            var Q31;
            {var subQ0=sQuery(id+"F2.wireOp",EDGE,"E50");Q31=makeQuery(id+"F2.imprint","IMPRINT",FACE,{"disambiguationData":[TD([[makeQuery(id+"F2.imprint","IMPRINT",EDGE,{"derivedFrom":subQ0}),-1.0]])]});}
            var Q32;
            {var subQ1=sQuery(id+"F2.wireOp",EDGE,"E48");Q32=makeQuery(id+"F2.imprint","IMPRINT",FACE,{"disambiguationData":[TD([[makeQuery(id+"F2.imprint","IMPRINT",EDGE,{"derivedFrom":subQ1}),-1.0]])]});}
            var Q33;
            {var subQ0=sQuery(id+"F2.wireOp",EDGE,"E47");Q33=makeQuery(id+"F2.imprint","IMPRINT",FACE,{"disambiguationData":[TD([[makeQuery(id+"F2.imprint","IMPRINT",EDGE,{"derivedFrom":subQ0}),1.0]])]});}
            var Q34;
            {var subQ4=sQuery(id+"F2.wireOp",EDGE,"E47");Q34=makeQuery(id+"F2.imprint","IMPRINT",FACE,{"disambiguationData":[TD([[makeQuery(id+"F2.imprint","IMPRINT",EDGE,{"derivedFrom":subQ4}),-1.0]])]});}
            var Q35;
            Q35=makeQuery(id+"F2.imprint","IMPRINT",FACE,{"disambiguationData":[TD([[makeQuery(id+"F2.imprint","IMPRINT",EDGE,{"derivedFrom":sQuery(id+"F2.wireOp",EDGE,"E39")}),-1.0]])]});
            var Q36;
            Q36=makeQuery(id+"F2.imprint","IMPRINT",FACE,{"disambiguationData":[TD([[makeQuery(id+"F2.imprint","IMPRINT",EDGE,{"derivedFrom":sQuery(id+"F2.wireOp",EDGE,"E37")}),-1.0]])]});
            var Q37;
            Q37=makeQuery(id+"F2.imprint","IMPRINT",FACE,{"disambiguationData":[TD([[makeQuery(id+"F2.imprint","IMPRINT",EDGE,{"derivedFrom":sQuery(id+"F2.wireOp",EDGE,"E35")}),-1.0]])]});
            var Q38;
            Q38=makeQuery(id+"F2.imprint","IMPRINT",FACE,{"disambiguationData":[TD([[makeQuery(id+"F2.imprint","IMPRINT",EDGE,{"derivedFrom":sQuery(id+"F2.wireOp",EDGE,"E33")}),-1.0]])]});
            var Q39;
            Q39=makeQuery(id+"F2.imprint","IMPRINT",FACE,{"disambiguationData":[TD([[makeQuery(id+"F2.imprint","IMPRINT",EDGE,{"derivedFrom":sQuery(id+"F2.wireOp",EDGE,"E41")}),1.0]])]});
            var Q40;
            Q40=makeQuery(id+"F2.imprint","IMPRINT",FACE,{"disambiguationData":[TD([[makeQuery(id+"F2.imprint","IMPRINT",EDGE,{"derivedFrom":sQuery(id+"F2.wireOp",EDGE,"E43")}),-1.0]])]});
            var Q41;
            Q41=makeQuery(id+"F2.imprint","IMPRINT",FACE,{"disambiguationData":[TD([[makeQuery(id+"F2.imprint","IMPRINT",EDGE,{"derivedFrom":sQuery(id+"F2.wireOp",EDGE,"E45")}),-1.0]])]});
            var Q42;
            Q42=makeQuery(id+"F2.imprint","IMPRINT",FACE,{"disambiguationData":[TD([[makeQuery(id+"F2.imprint","IMPRINT",EDGE,{"derivedFrom":sQuery(id+"F2.wireOp",EDGE,"E59.sketch_text.stroke-134")}),-1.0]])]});
            var Q43;
            Q43=makeQuery(id+"F2.imprint","IMPRINT",FACE,{"disambiguationData":[TD([[makeQuery(id+"F2.imprint","IMPRINT",EDGE,{"derivedFrom":sQuery(id+"F2.wireOp",EDGE,"E58.sketch_text.stroke-75")}),-1.0]])]});
            extrude(context, id + "F3", {"entities" : qUnion([Q0, Q1, Q2, Q3, Q4, Q5, Q6, Q7, Q8, Q9, Q10, Q11, Q12, Q13, Q14, Q15, Q16, Q17, Q18, Q19, Q20, Q21, Q22, Q23, Q24, Q25, Q26, Q27, Q28, Q29, Q30, Q31, Q32, Q33, Q34, Q35, Q36, Q37, Q38, Q39, Q40, Q41, Q42, Q43]), "depth" : .8 * mm, "offsetDistance" : 25 * mm});
        }
        {
            var Q0;
            Q0=makeQuery(id+"F3.opExtrude","CAP_FACE",FACE,{"disambiguationData":[OSD([sQuery(id+"F0.wireOp",EDGE,"E25"),sQuery(id+"F0.wireOp",EDGE,"E31"),sQuery(id+"F2.wireOp",EDGE,"E49"),sQuery(id+"F2.wireOp",EDGE,"E52"),sQuery(id+"F2.wireOp",EDGE,"E53"),sQuery(id+"F2.wireOp",EDGE,"E54"),sQuery(id+"F2.wireOp",EDGE,"E56")])],"isStart":false});
            var sketch = newSketch(context, id + "F4", { "sketchPlane" : qUnion([Q0])});
            skFitSpline(sketch, "E65", {"points": [v(0.84, 8.92) * mm, v(10.65, 2.03) * mm, v(25.9, -2.26) * mm], "startDerivative": vector(17.78, -17.12) * mm, "endDerivative": vector(27.14, -3.63) * mm});
            skFitSpline(sketch, "E66", {"points": [v(-1.58, 9.02) * mm, v(10.13, 0.84) * mm, v(25.71, -3.56) * mm], "startDerivative": vector(19.98, -21.9) * mm, "endDerivative": vector(27.82, -3.65) * mm});
            skFitSpline(sketch, "E67", {"points": [v(0.84, 8.92) * mm, v(12.83, 9.29) * mm, v(26.24, 12.26) * mm], "startDerivative": vector(25.56, -1.26) * mm, "endDerivative": vector(20.03, 5.21) * mm});
            skFitSpline(sketch, "E68", {"points": [v(-26.4, 0.3) * mm, v(-5.83, 2.89) * mm, v(12.24, -5.03) * mm], "startDerivative": vector(49.7, 29.2) * mm, "endDerivative": vector(34.07, -20.85) * mm});
            skFitSpline(sketch, "E69", {"points": [v(-26.4, -1.8) * mm, v(-5.83, 1.57) * mm, v(9.33, -5.03) * mm], "startDerivative": vector(41.22, 32.93) * mm, "endDerivative": vector(32.46, -15.17) * mm});
            skFitSpline(sketch, "E70", {"points": [v(-26.4, 19.33) * mm, v(-12.97, 11.65) * mm, v(-1.58, 9.02) * mm], "startDerivative": vector(29.42, -19.76) * mm, "endDerivative": vector(24.53, -2.4) * mm});
            skLineSegment(sketch, "E71", {"start": v(-26.4, -5.03) * mm, "end": v(25.6, -5.03) * mm});
            skLineSegment(sketch, "E72", {"start": v(25.6, 12.09) * mm, "end": v(25.6, -5.04) * mm});
            skLineSegment(sketch, "E73", {"start": v(-26.4, 19.3) * mm, "end": v(-26.4, -5.07) * mm});
            skSolve(sketch);
        }
        {
            var Q0;
            {var subQ9=sQuery(id+"F4.wireOp",EDGE,"E66");Q0=makeQuery(id+"F4.imprint","IMPRINT",FACE,{"disambiguationData":[TD([[makeQuery(id+"F4.imprint","IMPRINT",EDGE,{"derivedFrom":subQ9}),-1.0]])]});}
            var Q1;
            {var subQ2=sQuery(id+"F4.wireOp",EDGE,"E65");Q1=makeQuery(id+"F4.imprint","IMPRINT",FACE,{"disambiguationData":[TD([[makeQuery(id+"F4.imprint","IMPRINT",EDGE,{"derivedFrom":subQ2}),1.0]])]});}
            var Q2;
            {var subQ0=sQuery(id+"F4.wireOp",EDGE,"E69");Q2=makeQuery(id+"F4.imprint","IMPRINT",FACE,{"disambiguationData":[TD([[makeQuery(id+"F4.imprint","IMPRINT",EDGE,{"derivedFrom":subQ0}),-1.0]])]});}
            extrude(context, id + "F5", {"entities" : qUnion([Q0, Q1, Q2]), "depth" : .8 * mm, "offsetDistance" : 25 * mm});
        }
        {
            var Q0;
            Q0=qCreatedBy(makeId("Top.planeOp"),FACE);
            var Q1;
            Q1 = qBodyType(qCreatedBy(id + "F7" ,EDGE), BodyType.WIRE);
            cPlane(context, id + "F6", {"entities" : qUnion([Q0, Q1]), "cplaneType" : CPlaneType.OFFSET, "offset" : .15 * mm, "width" : 150 * mm, "height" : 150 * mm});
        }
        {
            var Q0;
            Q0=qCreatedBy(id+"F6.planeOp",FACE);
            var sketch = newSketch(context, id + "F7", { "sketchPlane" : qUnion([Q0])});
            skCircle(sketch, "E74", {"center": v(0.2, 37.1) * mm, "radius": 4 * mm});
            skCircle(sketch, "E75", {"center": v(-0.04, -16.34) * mm, "radius": 4 * mm});
            skSolve(sketch);
        }
        {
            var Q0;
            Q0=qSketchRegion(id+"F7",true);
            extrude(context, id + "F8", {"entities" : qUnion([Q0]), "operationType" : NewBodyOperationType.REMOVE, "depth" : 2 * mm, "offsetDistance" : 25 * mm});
        }
    });
